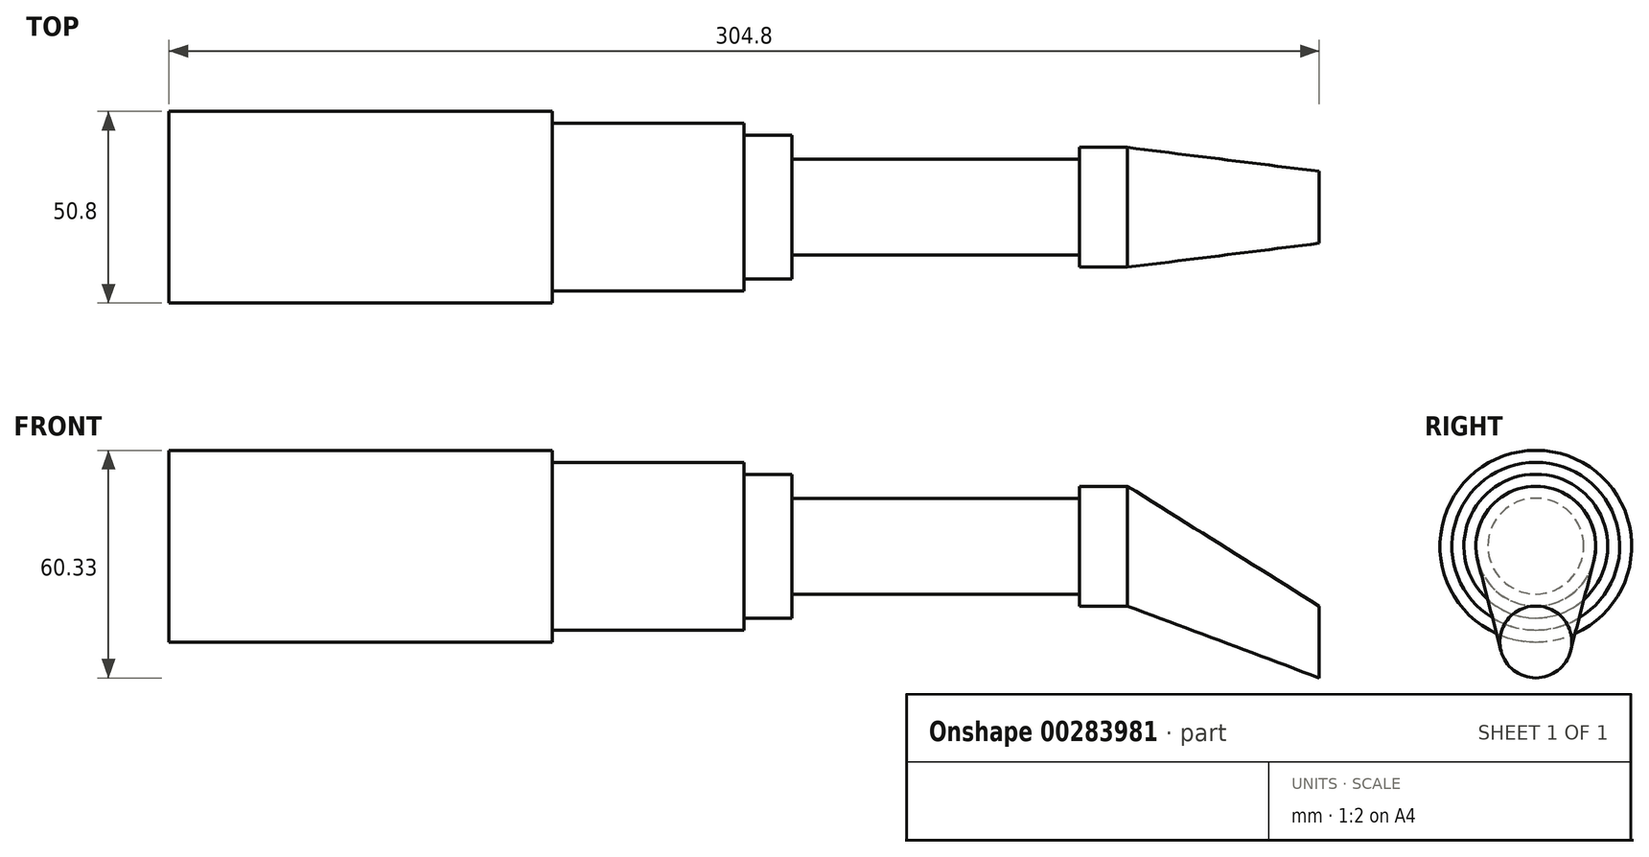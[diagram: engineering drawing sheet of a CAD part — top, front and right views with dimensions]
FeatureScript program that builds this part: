
annotation { "Feature Type Name" : "Feature", "Feature Type Description" : "" }
export const myFeature = defineFeature(function(context is Context, id is Id, definition is map)
    precondition{}
    {
        {
            var Q0;
            Q0=qCreatedBy(makeId("Right.planeOp"),FACE);
            var sketch = newSketch(context, id + "F0", { "sketchPlane" : qUnion([Q0])});
            skCircle(sketch, "E0", {"center": v(0, 0) * mm, "radius": 25.4 * mm});
            skCircle(sketch, "E1", {"center": v(0, 0) * mm, "radius": 19.05 * mm});
            skCircle(sketch, "E2", {"center": v(0, 0) * mm, "radius": 22.23 * mm});
            skSolve(sketch);
        }
        {
            var Q0;
            Q0=makeQuery(id+"F0.imprint","IMPRINT",FACE,{"disambiguationData":[TD([[makeQuery(id+"F0.imprint","IMPRINT",EDGE,{"derivedFrom":sQuery(id+"F0.wireOp",EDGE,"E0")}),1.0]])]});
            extrude(context, id + "F1", {"entities" : qUnion([Q0]), "depth" : 101.6 * mm});
        }
        {
            var Q0;
            Q0=makeQuery(id+"F0.imprint","IMPRINT",FACE,{"disambiguationData":[TD([[makeQuery(id+"F0.imprint","IMPRINT",EDGE,{"derivedFrom":sQuery(id+"F0.wireOp",EDGE,"E1")}),-1.0]])]});
            extrude(context, id + "F2", {"entities" : qUnion([Q0]), "operationType" : NewBodyOperationType.ADD, "depth" : 152.4 * mm});
        }
        {
            var Q0;
            Q0=makeQuery(id+"F0.imprint","IMPRINT",FACE,{"disambiguationData":[TD([[makeQuery(id+"F0.imprint","IMPRINT",EDGE,{"derivedFrom":sQuery(id+"F0.wireOp",EDGE,"E1")}),1.0]])]});
            extrude(context, id + "F3", {"entities" : qUnion([Q0]), "operationType" : NewBodyOperationType.ADD, "depth" : 165.1 * mm});
        }
        {
            var Q0;
            Q0=makeQuery(id+"F3.opExtrude","CAP_FACE",FACE,{"disambiguationData":[OSD([sQuery(id+"F0.wireOp",EDGE,"E1")])],"isStart":false});
            var sketch = newSketch(context, id + "F4", { "sketchPlane" : qUnion([Q0])});
            skCircle(sketch, "E3", {"center": v(0, 0) * mm, "radius": 12.7 * mm});
            skSolve(sketch);
        }
        {
            var Q0;
            Q0=makeQuery(id+"F4.imprint","IMPRINT",FACE,{"disambiguationData":[TD([[makeQuery(id+"F4.imprint","IMPRINT",EDGE,{"derivedFrom":sQuery(id+"F4.wireOp",EDGE,"E3")}),1.0]])]});
            extrude(context, id + "F5", {"entities" : qUnion([Q0]), "operationType" : NewBodyOperationType.ADD, "depth" : 76.2 * mm});
        }
        {
            var Q0;
            Q0=qCreatedBy(makeId("Right.planeOp"),FACE);
            cPlane(context, id + "F6", {"entities" : qUnion([Q0]), "cplaneType" : CPlaneType.OFFSET, "offset" : 304.8 * mm, "width" : 152.4 * mm, "height" : 152.4 * mm});
        }
        {
            var Q0;
            Q0=qCreatedBy(id+"F6.planeOp",FACE);
            var sketch = newSketch(context, id + "F7", { "sketchPlane" : qUnion([Q0])});
            skCircle(sketch, "E4", {"center": v(0, -25.4) * mm, "radius": 9.53 * mm});
            skSolve(sketch);
        }
        {
            var Q0;
            Q0=makeQuery(id+"F5.opExtrude","CAP_FACE",FACE,{"disambiguationData":[OSD([sQuery(id+"F4.wireOp",EDGE,"E3")])],"isStart":false});
            var sketch = newSketch(context, id + "F8", { "sketchPlane" : qUnion([Q0])});
            skCircle(sketch, "E5", {"center": v(0, 0) * mm, "radius": 15.88 * mm});
            skSolve(sketch);
        }
        {
            var Q0;
            Q0=makeQuery(id+"F8.imprint","IMPRINT",FACE,{"disambiguationData":[TD([[makeQuery(id+"F8.imprint","IMPRINT",EDGE,{"derivedFrom":sQuery(id+"F8.wireOp",EDGE,"E5")}),1.0]])]});
            var Q1;
            Q1=makeQuery(id+"F8.imprint","IMPRINT",FACE,{"disambiguationData":[TD([[makeQuery(id+"F8.imprint","IMPRINT",EDGE,{"derivedFrom":makeQuery(id+"F5.opExtrude","CAP_EDGE",EDGE,{"disambiguationData":[OSD([sQuery(id+"F4.wireOp",EDGE,"E3")])],"isStart":false})}),1.0]])]});
            extrude(context, id + "F9", {"entities" : qUnion([Q0, Q1]), "operationType" : NewBodyOperationType.ADD, "depth" : 12.7 * mm});
        }
        {
            var Q0;
            Q0=makeQuery(id+"F7.imprint","IMPRINT",FACE,{"disambiguationData":[TD([[makeQuery(id+"F7.imprint","IMPRINT",EDGE,{"derivedFrom":sQuery(id+"F7.wireOp",EDGE,"E4")}),1.0]])]});
            var Q1;
            Q1=makeQuery(id+"F9.opExtrude","CAP_FACE",FACE,{"disambiguationData":[OSD([sQuery(id+"F8.wireOp",EDGE,"E5")])],"isStart":false});
            loft(context, id + "F10", {"sheetProfilesArray" : [{ "sheetProfileEntities" : qUnion([Q0]) }, { "sheetProfileEntities" : qUnion([Q1]) }]});
        }
    });
